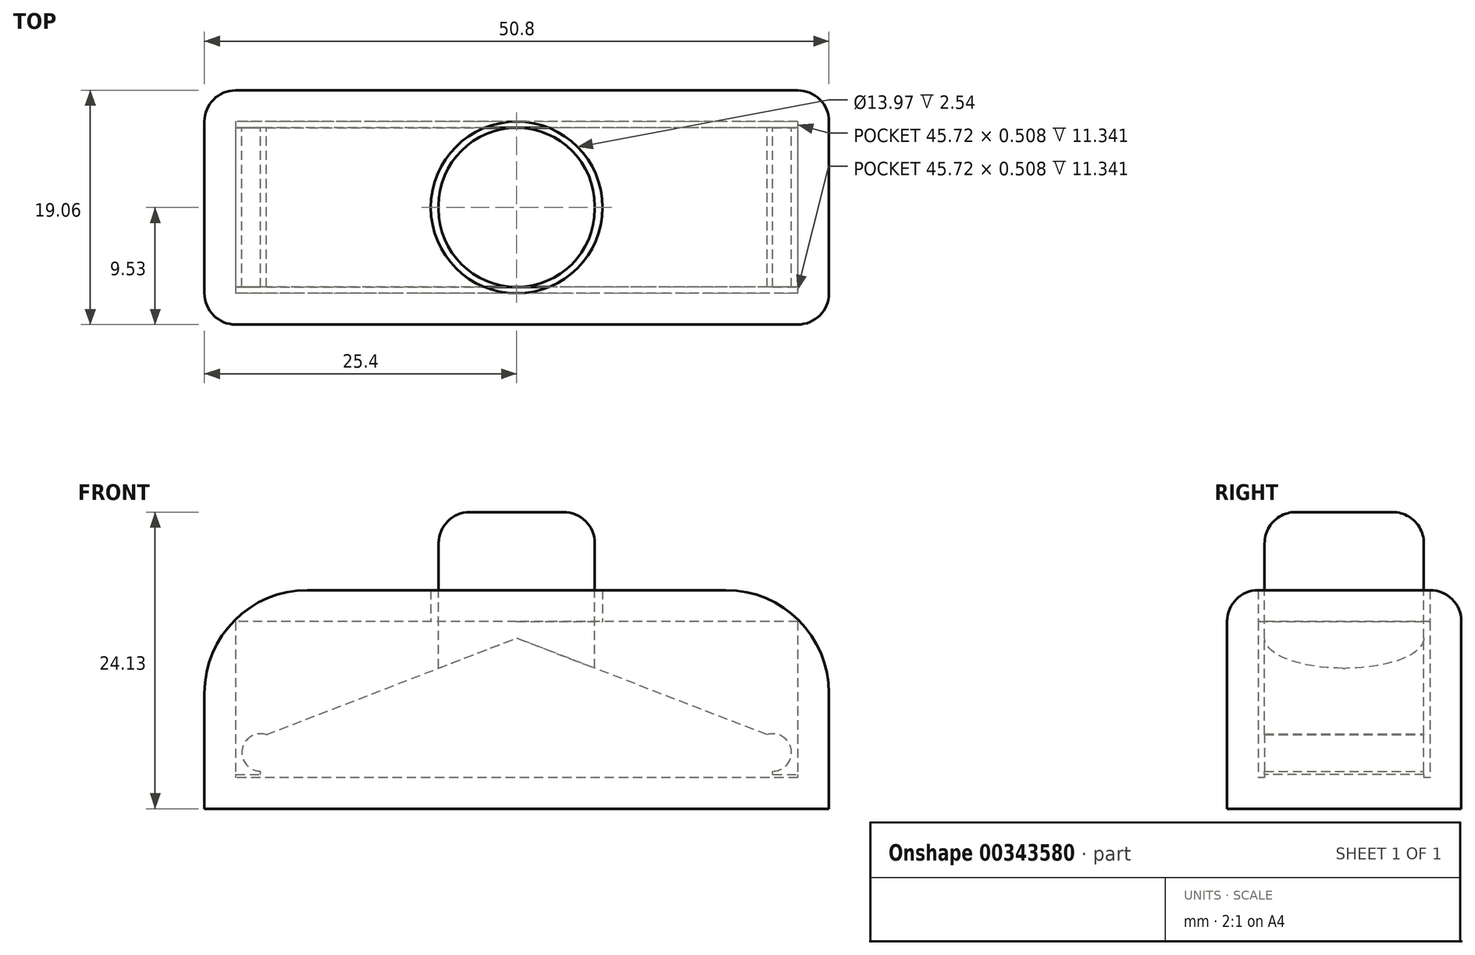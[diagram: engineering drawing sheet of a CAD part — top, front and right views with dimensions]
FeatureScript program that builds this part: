
annotation { "Feature Type Name" : "Feature", "Feature Type Description" : "" }
export const myFeature = defineFeature(function(context is Context, id is Id, definition is map)
    precondition{}
    {
        {
            var Q0;
            Q0=qCreatedBy(makeId("Top.planeOp"),FACE);
            var sketch = newSketch(context, id + "F0", { "sketchPlane" : qUnion([Q0])});
            skLineSegment(sketch, "E0.bottom", {"start": v(25.4, 9.53) * mm, "end": v(-25.4, 9.53) * mm});
            skLineSegment(sketch, "E0.top", {"start": v(25.4, -9.53) * mm, "end": v(-25.4, -9.53) * mm});
            skLineSegment(sketch, "E0.left", {"start": v(25.4, 9.53) * mm, "end": v(25.4, -9.53) * mm});
            skLineSegment(sketch, "E0.right", {"start": v(-25.4, 9.53) * mm, "end": v(-25.4, -9.53) * mm});
            skPoint(sketch, "E0.middle", {"position": v(0, 0) * mm});
            skLineSegment(sketch, "E1.bottom", {"start": v(22.86, 6.99) * mm, "end": v(-22.86, 6.99) * mm});
            skLineSegment(sketch, "E1.top", {"start": v(22.86, -6.99) * mm, "end": v(-22.86, -6.99) * mm});
            skLineSegment(sketch, "E1.left", {"start": v(22.86, 6.98) * mm, "end": v(22.86, -6.99) * mm});
            skLineSegment(sketch, "E1.right", {"start": v(-22.86, 6.99) * mm, "end": v(-22.86, -6.98) * mm});
            skSolve(sketch);
        }
        {
            var Q0;
            Q0 = qSketchRegion(id + "F0", true);
            extrude(context, id + "F1", {"entities" : qUnion([Q0]), "depth" : 12.7 * mm, "offsetDistance" : 25.4 * mm});
        }
        {
            var Q0;
            Q0=makeQuery(id+"F1.opExtrude","CAP_FACE",FACE,{"disambiguationData":[OSD([sQuery(id+"F0.wireOp",EDGE,"E0.bottom"),sQuery(id+"F0.wireOp",EDGE,"E0.top"),sQuery(id+"F0.wireOp",EDGE,"E0.left"),sQuery(id+"F0.wireOp",EDGE,"E0.right"),sQuery(id+"F0.wireOp",EDGE,"E1.bottom"),sQuery(id+"F0.wireOp",EDGE,"E1.top"),sQuery(id+"F0.wireOp",EDGE,"E1.left"),sQuery(id+"F0.wireOp",EDGE,"E1.right")])],"isStart":true});
            var sketch = newSketch(context, id + "F2", { "sketchPlane" : qUnion([Q0])});
            skLineSegment(sketch, "E2.bottom", {"start": v(25.4, 9.53) * mm, "end": v(-25.4, 9.53) * mm});
            skLineSegment(sketch, "E2.top", {"start": v(25.4, -9.53) * mm, "end": v(-25.4, -9.53) * mm});
            skLineSegment(sketch, "E2.left", {"start": v(25.4, 9.53) * mm, "end": v(25.4, -9.53) * mm});
            skLineSegment(sketch, "E2.right", {"start": v(-25.4, 9.53) * mm, "end": v(-25.4, -9.53) * mm});
            skSolve(sketch);
        }
        {
            var Q0;
            Q0 = qSketchRegion(id + "F2", true);
            extrude(context, id + "F3", {"entities" : qUnion([Q0]), "operationType" : NewBodyOperationType.ADD, "depth" : 2.54 * mm, "offsetDistance" : 25.4 * mm});
        }
        {
            var Q0;
            Q0=makeQuery(id+"F1.opExtrude","SWEPT_FACE",FACE,{"disambiguationData":[OSD([sQuery(id+"F0.wireOp",EDGE,"E1.bottom")])]});
            var sketch = newSketch(context, id + "F4", { "sketchPlane" : qUnion([Q0])});
            skLineSegment(sketch, "E3.bottom", {"start": v(-25.4, -2.54) * mm, "end": v(25.4, -2.54) * mm});
            skLineSegment(sketch, "E3.top", {"start": v(-25.4, -2.54) * mm, "end": v(25.4, -2.54) * mm});
            skLineSegment(sketch, "E3.left", {"start": v(-25.4, -2.54) * mm, "end": v(-25.4, -2.54) * mm});
            skLineSegment(sketch, "E3.right", {"start": v(25.4, -2.54) * mm, "end": v(25.4, -2.54) * mm});
            skLineSegment(sketch, "E4.top", {"start": v(-25.4, 0.25) * mm, "end": v(25.4, 0.25) * mm});
            skLineSegment(sketch, "E4.left", {"start": v(-25.4, -2.54) * mm, "end": v(-25.4, 0.25) * mm});
            skLineSegment(sketch, "E4.right", {"start": v(25.4, -2.54) * mm, "end": v(25.4, 0.25) * mm});
            skLineSegment(sketch, "E5", {"start": v(25.4, 12.7) * mm, "end": v(-25.4, 12.7) * mm});
            skLineSegment(sketch, "E6.bottom", {"start": v(6.35, 7.62) * mm, "end": v(-6.35, 7.62) * mm});
            skLineSegment(sketch, "E6.top", {"start": v(6.35, 17.78) * mm, "end": v(-6.35, 17.78) * mm});
            skLineSegment(sketch, "E6.left", {"start": v(6.35, 7.62) * mm, "end": v(6.35, 17.78) * mm});
            skLineSegment(sketch, "E6.right", {"start": v(-6.35, 7.62) * mm, "end": v(-6.35, 17.78) * mm});
            skPoint(sketch, "E6.middle", {"position": v(0, 12.7) * mm});
            skLineSegment(sketch, "E7", {"start": v(6.35, 7.62) * mm, "end": v(5.08, 7.62) * mm});
            skLineSegment(sketch, "E8", {"start": v(6.35, 7.62) * mm, "end": v(6.35, 8.89) * mm});
            skLineSegment(sketch, "E9", {"start": v(-6.35, 7.62) * mm, "end": v(-5.08, 7.62) * mm});
            skLineSegment(sketch, "E10", {"start": v(-6.35, 7.62) * mm, "end": v(-6.35, 8.89) * mm});
            skLineSegment(sketch, "E11", {"start": v(-25.4, 0.25) * mm, "end": v(-20.83, 0.25) * mm});
            skLineSegment(sketch, "E12", {"start": v(-20.83, 0.25) * mm, "end": v(-20.83, 2.03) * mm});
            skCircle(sketch, "E13", {"center": v(-20.83, 2.03) * mm, "radius": 1.52 * mm});
            skLineSegment(sketch, "E14", {"start": v(-20.83, 2.03) * mm, "end": v(-19.56, 2.03) * mm});
            skLineSegment(sketch, "E15", {"start": v(-20.83, 2.03) * mm, "end": v(-20.83, 3.3) * mm});
            skLineSegment(sketch, "E16", {"start": v(-20.83, 3.3) * mm, "end": v(-6.35, 8.89) * mm});
            skLineSegment(sketch, "E17", {"start": v(25.4, -2.54) * mm, "end": v(20.83, -2.54) * mm});
            skLineSegment(sketch, "E18", {"start": v(20.83, -2.54) * mm, "end": v(20.83, 2.03) * mm});
            skCircle(sketch, "E19", {"center": v(20.83, 2.03) * mm, "radius": 1.52 * mm});
            skLineSegment(sketch, "E20", {"start": v(20.83, 2.03) * mm, "end": v(20.83, 3.3) * mm});
            skLineSegment(sketch, "E21", {"start": v(20.83, 2.03) * mm, "end": v(19.56, 2.03) * mm});
            skLineSegment(sketch, "E22", {"start": v(20.83, 3.3) * mm, "end": v(6.35, 8.89) * mm});
            skLineSegment(sketch, "E23", {"start": v(19.56, 2.03) * mm, "end": v(5.08, 7.62) * mm});
            skLineSegment(sketch, "E24", {"start": v(-19.56, 2.03) * mm, "end": v(-5.08, 7.62) * mm});
            skLineSegment(sketch, "E25.bottom", {"start": v(-6.35, 17.78) * mm, "end": v(6.35, 17.78) * mm});
            skLineSegment(sketch, "E25.top", {"start": v(-6.35, 21.59) * mm, "end": v(6.35, 21.59) * mm});
            skLineSegment(sketch, "E25.left", {"start": v(-6.35, 17.78) * mm, "end": v(-6.35, 21.59) * mm});
            skLineSegment(sketch, "E25.right", {"start": v(6.35, 17.78) * mm, "end": v(6.35, 21.59) * mm});
            skSolve(sketch);
        }
        {
            var Q0;
            Q0 = qSketchRegion(id + "F4", true);
            extrude(context, id + "F5", {"entities" : qUnion([Q0]), "operationType" : NewBodyOperationType.ADD, "depth" : 13.46 * mm, "offsetDistance" : 25.4 * mm, "hasSecondDirection" : true, "secondDirectionOppositeDirection" : true, "secondDirectionDepth" : -0.5 * mm});
        }
        {
            var Q0;
            Q0=makeQuery(id+"F5.opExtrude","CAP_EDGE",EDGE,{"disambiguationData":[OSD([sQuery(id+"F4.wireOp",EDGE,"E6.right")])],"isStart":false});
            var Q1;
            Q1=makeQuery(id+"F5.opExtrude","CAP_EDGE",EDGE,{"disambiguationData":[OSD([sQuery(id+"F4.wireOp",EDGE,"E6.left")])],"isStart":false});
            var Q2;
            Q2=makeQuery(id+"F5.opExtrude","CAP_EDGE",EDGE,{"disambiguationData":[OSD([sQuery(id+"F4.wireOp",EDGE,"E6.left")])],"isStart":true});
            var Q3;
            Q3=makeQuery(id+"F5.opExtrude","CAP_EDGE",EDGE,{"disambiguationData":[OSD([sQuery(id+"F4.wireOp",EDGE,"E6.right")])],"isStart":true});
            fillet(context, id + "F6", {"entities" : qUnion([Q0, Q1, Q2, Q3]), "tangentPropagation" : true, "radius" : 6.35 * mm, "defaultsChanged" : true, "vertexSettings" : [], "allowEdgeOverflow" : false});
        }
        {
            var Q0;
            Q0=makeQuery(id+"F1.opExtrude","CAP_FACE",FACE,{"disambiguationData":[OSD([sQuery(id+"F0.wireOp",EDGE,"E0.bottom"),sQuery(id+"F0.wireOp",EDGE,"E0.top"),sQuery(id+"F0.wireOp",EDGE,"E0.left"),sQuery(id+"F0.wireOp",EDGE,"E0.right"),sQuery(id+"F0.wireOp",EDGE,"E1.bottom"),sQuery(id+"F0.wireOp",EDGE,"E1.top"),sQuery(id+"F0.wireOp",EDGE,"E1.left"),sQuery(id+"F0.wireOp",EDGE,"E1.right")])],"isStart":false});
            var sketch = newSketch(context, id + "F7", { "sketchPlane" : qUnion([Q0])});
            skLineSegment(sketch, "E26.bottom", {"start": v(-25.4, 9.53) * mm, "end": v(25.4, 9.53) * mm});
            skLineSegment(sketch, "E26.top", {"start": v(-25.4, -9.53) * mm, "end": v(25.4, -9.53) * mm});
            skLineSegment(sketch, "E26.left", {"start": v(-25.4, 9.53) * mm, "end": v(-25.4, -9.53) * mm});
            skLineSegment(sketch, "E26.right", {"start": v(25.4, 9.53) * mm, "end": v(25.4, -9.53) * mm});
            skCircle(sketch, "E27", {"center": v(0, 0) * mm, "radius": 6.99 * mm});
            skSolve(sketch);
        }
        {
            var Q0;
            Q0 = qSketchRegion(id + "F7", true);
            extrude(context, id + "F8", {"entities" : qUnion([Q0]), "operationType" : NewBodyOperationType.ADD, "depth" : 2.54 * mm, "offsetDistance" : 25.4 * mm});
        }
        {
            var Q0;
            Q0=makeQuery(id+"F6.opFillet","BLEND_EDGE",EDGE,{"blendedFrom":[makeQuery(id+"F5.opExtrude","CAP_EDGE",EDGE,{"disambiguationData":[OSD([sQuery(id+"F4.wireOp",EDGE,"E6.left"),sQuery(id+"F4.wireOp",EDGE,"E25.right")])],"isStart":false}),makeQuery(id+"F5.opExtrude","SWEPT_FACE",FACE,{"disambiguationData":[OSD([sQuery(id+"F4.wireOp",EDGE,"E25.top")])]})],"blendedInto":[makeQuery(id+"F5.opExtrude","SWEPT_FACE",FACE,{"disambiguationData":[OSD([sQuery(id+"F4.wireOp",EDGE,"E25.top")])]})]});
            fillet(context, id + "F9", {"entities" : qUnion([Q0]), "tangentPropagation" : true, "radius" : 2.54 * mm, "defaultsChanged" : true, "vertexSettings" : [], "allowEdgeOverflow" : false});
        }
        {
            var Q0;
            Q0=makeQuery(id+"F8.opExtrude","CAP_EDGE",EDGE,{"disambiguationData":[OSD([sQuery(id+"F7.wireOp",EDGE,"E26.right")])],"isStart":false});
            var Q1;
            Q1=makeQuery(id+"F8.opExtrude","CAP_EDGE",EDGE,{"disambiguationData":[OSD([sQuery(id+"F7.wireOp",EDGE,"E26.left")])],"isStart":false});
            fillet(context, id + "F10", {"entities" : qUnion([Q0, Q1]), "tangentPropagation" : true, "radius" : 8.38 * mm, "defaultsChanged" : true, "vertexSettings" : [], "allowEdgeOverflow" : false});
        }
        {
            var Q0;
            Q0=makeQuery(id+"F8.opExtrude","CAP_EDGE",EDGE,{"disambiguationData":[OSD([sQuery(id+"F7.wireOp",EDGE,"E26.bottom")])],"isStart":false});
            var Q1;
            Q1=makeQuery(id+"F8.opExtrude","CAP_EDGE",EDGE,{"disambiguationData":[OSD([sQuery(id+"F7.wireOp",EDGE,"E26.top")])],"isStart":false});
            var Q2;
            Q2=makeQuery(id+"F10.opFillet","BLEND_EDGE",EDGE,{"blendedFrom":[makeQuery(id+"F8.opExtrude","CAP_EDGE",EDGE,{"disambiguationData":[OSD([sQuery(id+"F7.wireOp",EDGE,"E26.left")])],"isStart":false}),makeQuery(id+"F8.boolean.opBoolean","MERGE",FACE,{"derivedFrom":[makeQuery(id+"F3.boolean.opBoolean","MERGE",FACE,{"derivedFrom":[makeQuery(id+"F1.opExtrude","SWEPT_FACE",FACE,{"disambiguationData":[OSD([sQuery(id+"F0.wireOp",EDGE,"E0.top")])]}),makeQuery(id+"F3.opExtrude","SWEPT_FACE",FACE,{"disambiguationData":[OSD([sQuery(id+"F2.wireOp",EDGE,"E2.bottom")])]})]}),makeQuery(id+"F8.opExtrude","SWEPT_FACE",FACE,{"disambiguationData":[OSD([sQuery(id+"F7.wireOp",EDGE,"E26.top")])]})]})],"blendedInto":[makeQuery(id+"F8.boolean.opBoolean","MERGE",FACE,{"derivedFrom":[makeQuery(id+"F3.boolean.opBoolean","MERGE",FACE,{"derivedFrom":[makeQuery(id+"F1.opExtrude","SWEPT_FACE",FACE,{"disambiguationData":[OSD([sQuery(id+"F0.wireOp",EDGE,"E0.top")])]}),makeQuery(id+"F3.opExtrude","SWEPT_FACE",FACE,{"disambiguationData":[OSD([sQuery(id+"F2.wireOp",EDGE,"E2.bottom")])]})]}),makeQuery(id+"F8.opExtrude","SWEPT_FACE",FACE,{"disambiguationData":[OSD([sQuery(id+"F7.wireOp",EDGE,"E26.top")])]})]})]});
            var Q3;
            Q3=makeQuery(id+"F10.opFillet","BLEND_EDGE",EDGE,{"blendedFrom":[makeQuery(id+"F8.opExtrude","CAP_EDGE",EDGE,{"disambiguationData":[OSD([sQuery(id+"F7.wireOp",EDGE,"E26.left")])],"isStart":false}),makeQuery(id+"F8.boolean.opBoolean","MERGE",FACE,{"derivedFrom":[makeQuery(id+"F3.boolean.opBoolean","MERGE",FACE,{"derivedFrom":[makeQuery(id+"F1.opExtrude","SWEPT_FACE",FACE,{"disambiguationData":[OSD([sQuery(id+"F0.wireOp",EDGE,"E0.bottom")])]}),makeQuery(id+"F3.opExtrude","SWEPT_FACE",FACE,{"disambiguationData":[OSD([sQuery(id+"F2.wireOp",EDGE,"E2.top")])]})]}),makeQuery(id+"F8.opExtrude","SWEPT_FACE",FACE,{"disambiguationData":[OSD([sQuery(id+"F7.wireOp",EDGE,"E26.bottom")])]})]})],"blendedInto":[makeQuery(id+"F8.boolean.opBoolean","MERGE",FACE,{"derivedFrom":[makeQuery(id+"F3.boolean.opBoolean","MERGE",FACE,{"derivedFrom":[makeQuery(id+"F1.opExtrude","SWEPT_FACE",FACE,{"disambiguationData":[OSD([sQuery(id+"F0.wireOp",EDGE,"E0.bottom")])]}),makeQuery(id+"F3.opExtrude","SWEPT_FACE",FACE,{"disambiguationData":[OSD([sQuery(id+"F2.wireOp",EDGE,"E2.top")])]})]}),makeQuery(id+"F8.opExtrude","SWEPT_FACE",FACE,{"disambiguationData":[OSD([sQuery(id+"F7.wireOp",EDGE,"E26.bottom")])]})]})]});
            var Q4;
            Q4=makeQuery(id+"F8.boolean.opBoolean","MERGE",EDGE,{"derivedFrom":[makeQuery(id+"F3.boolean.opBoolean","MERGE",EDGE,{"derivedFrom":[makeQuery(id+"F1.opExtrude","SWEPT_EDGE",EDGE,{"disambiguationData":[OSD([sQuery(id+"F0.wireOp",EDGE,"E0.bottom"),sQuery(id+"F0.wireOp",EDGE,"E0.right")])]}),makeQuery(id+"F3.opExtrude","SWEPT_EDGE",EDGE,{"disambiguationData":[OSD([sQuery(id+"F2.wireOp",EDGE,"E2.top"),sQuery(id+"F2.wireOp",EDGE,"E2.right")])]})]}),makeQuery(id+"F8.opExtrude","SWEPT_EDGE",EDGE,{"disambiguationData":[OSD([sQuery(id+"F7.wireOp",EDGE,"E26.bottom"),sQuery(id+"F7.wireOp",EDGE,"E26.left")])]})]});
            var Q5;
            Q5=makeQuery(id+"F8.boolean.opBoolean","MERGE",EDGE,{"derivedFrom":[makeQuery(id+"F3.boolean.opBoolean","MERGE",EDGE,{"derivedFrom":[makeQuery(id+"F1.opExtrude","SWEPT_EDGE",EDGE,{"disambiguationData":[OSD([sQuery(id+"F0.wireOp",EDGE,"E0.top"),sQuery(id+"F0.wireOp",EDGE,"E0.right")])]}),makeQuery(id+"F3.opExtrude","SWEPT_EDGE",EDGE,{"disambiguationData":[OSD([sQuery(id+"F2.wireOp",EDGE,"E2.bottom"),sQuery(id+"F2.wireOp",EDGE,"E2.right")])]})]}),makeQuery(id+"F8.opExtrude","SWEPT_EDGE",EDGE,{"disambiguationData":[OSD([sQuery(id+"F7.wireOp",EDGE,"E26.top"),sQuery(id+"F7.wireOp",EDGE,"E26.left")])]})]});
            var Q6;
            Q6=makeQuery(id+"F8.boolean.opBoolean","MERGE",EDGE,{"derivedFrom":[makeQuery(id+"F3.boolean.opBoolean","MERGE",EDGE,{"derivedFrom":[makeQuery(id+"F1.opExtrude","SWEPT_EDGE",EDGE,{"disambiguationData":[OSD([sQuery(id+"F0.wireOp",EDGE,"E0.bottom"),sQuery(id+"F0.wireOp",EDGE,"E0.left")])]}),makeQuery(id+"F3.opExtrude","SWEPT_EDGE",EDGE,{"disambiguationData":[OSD([sQuery(id+"F2.wireOp",EDGE,"E2.top"),sQuery(id+"F2.wireOp",EDGE,"E2.left")])]})]}),makeQuery(id+"F8.opExtrude","SWEPT_EDGE",EDGE,{"disambiguationData":[OSD([sQuery(id+"F7.wireOp",EDGE,"E26.bottom"),sQuery(id+"F7.wireOp",EDGE,"E26.right")])]})]});
            var Q7;
            Q7=makeQuery(id+"F10.opFillet","BLEND_EDGE",EDGE,{"blendedFrom":[makeQuery(id+"F8.opExtrude","CAP_EDGE",EDGE,{"disambiguationData":[OSD([sQuery(id+"F7.wireOp",EDGE,"E26.right")])],"isStart":false}),makeQuery(id+"F8.boolean.opBoolean","MERGE",FACE,{"derivedFrom":[makeQuery(id+"F3.boolean.opBoolean","MERGE",FACE,{"derivedFrom":[makeQuery(id+"F1.opExtrude","SWEPT_FACE",FACE,{"disambiguationData":[OSD([sQuery(id+"F0.wireOp",EDGE,"E0.bottom")])]}),makeQuery(id+"F3.opExtrude","SWEPT_FACE",FACE,{"disambiguationData":[OSD([sQuery(id+"F2.wireOp",EDGE,"E2.top")])]})]}),makeQuery(id+"F8.opExtrude","SWEPT_FACE",FACE,{"disambiguationData":[OSD([sQuery(id+"F7.wireOp",EDGE,"E26.bottom")])]})]})],"blendedInto":[makeQuery(id+"F8.boolean.opBoolean","MERGE",FACE,{"derivedFrom":[makeQuery(id+"F3.boolean.opBoolean","MERGE",FACE,{"derivedFrom":[makeQuery(id+"F1.opExtrude","SWEPT_FACE",FACE,{"disambiguationData":[OSD([sQuery(id+"F0.wireOp",EDGE,"E0.bottom")])]}),makeQuery(id+"F3.opExtrude","SWEPT_FACE",FACE,{"disambiguationData":[OSD([sQuery(id+"F2.wireOp",EDGE,"E2.top")])]})]}),makeQuery(id+"F8.opExtrude","SWEPT_FACE",FACE,{"disambiguationData":[OSD([sQuery(id+"F7.wireOp",EDGE,"E26.bottom")])]})]})]});
            var Q8;
            Q8=makeQuery(id+"F10.opFillet","BLEND_EDGE",EDGE,{"blendedFrom":[makeQuery(id+"F8.opExtrude","CAP_EDGE",EDGE,{"disambiguationData":[OSD([sQuery(id+"F7.wireOp",EDGE,"E26.right")])],"isStart":false}),makeQuery(id+"F8.boolean.opBoolean","MERGE",FACE,{"derivedFrom":[makeQuery(id+"F3.boolean.opBoolean","MERGE",FACE,{"derivedFrom":[makeQuery(id+"F1.opExtrude","SWEPT_FACE",FACE,{"disambiguationData":[OSD([sQuery(id+"F0.wireOp",EDGE,"E0.top")])]}),makeQuery(id+"F3.opExtrude","SWEPT_FACE",FACE,{"disambiguationData":[OSD([sQuery(id+"F2.wireOp",EDGE,"E2.bottom")])]})]}),makeQuery(id+"F8.opExtrude","SWEPT_FACE",FACE,{"disambiguationData":[OSD([sQuery(id+"F7.wireOp",EDGE,"E26.top")])]})]})],"blendedInto":[makeQuery(id+"F8.boolean.opBoolean","MERGE",FACE,{"derivedFrom":[makeQuery(id+"F3.boolean.opBoolean","MERGE",FACE,{"derivedFrom":[makeQuery(id+"F1.opExtrude","SWEPT_FACE",FACE,{"disambiguationData":[OSD([sQuery(id+"F0.wireOp",EDGE,"E0.top")])]}),makeQuery(id+"F3.opExtrude","SWEPT_FACE",FACE,{"disambiguationData":[OSD([sQuery(id+"F2.wireOp",EDGE,"E2.bottom")])]})]}),makeQuery(id+"F8.opExtrude","SWEPT_FACE",FACE,{"disambiguationData":[OSD([sQuery(id+"F7.wireOp",EDGE,"E26.top")])]})]})]});
            var Q9;
            Q9=makeQuery(id+"F8.boolean.opBoolean","MERGE",EDGE,{"derivedFrom":[makeQuery(id+"F3.boolean.opBoolean","MERGE",EDGE,{"derivedFrom":[makeQuery(id+"F1.opExtrude","SWEPT_EDGE",EDGE,{"disambiguationData":[OSD([sQuery(id+"F0.wireOp",EDGE,"E0.top"),sQuery(id+"F0.wireOp",EDGE,"E0.left")])]}),makeQuery(id+"F3.opExtrude","SWEPT_EDGE",EDGE,{"disambiguationData":[OSD([sQuery(id+"F2.wireOp",EDGE,"E2.bottom"),sQuery(id+"F2.wireOp",EDGE,"E2.left")])]})]}),makeQuery(id+"F8.opExtrude","SWEPT_EDGE",EDGE,{"disambiguationData":[OSD([sQuery(id+"F7.wireOp",EDGE,"E26.top"),sQuery(id+"F7.wireOp",EDGE,"E26.right")])]})]});
            fillet(context, id + "F11", {"entities" : qUnion([Q0, Q1, Q2, Q3, Q4, Q5, Q6, Q7, Q8, Q9]), "tangentPropagation" : true, "radius" : 2.54 * mm, "defaultsChanged" : false, "vertexSettings" : [], "allowEdgeOverflow" : false});
        }
    });
